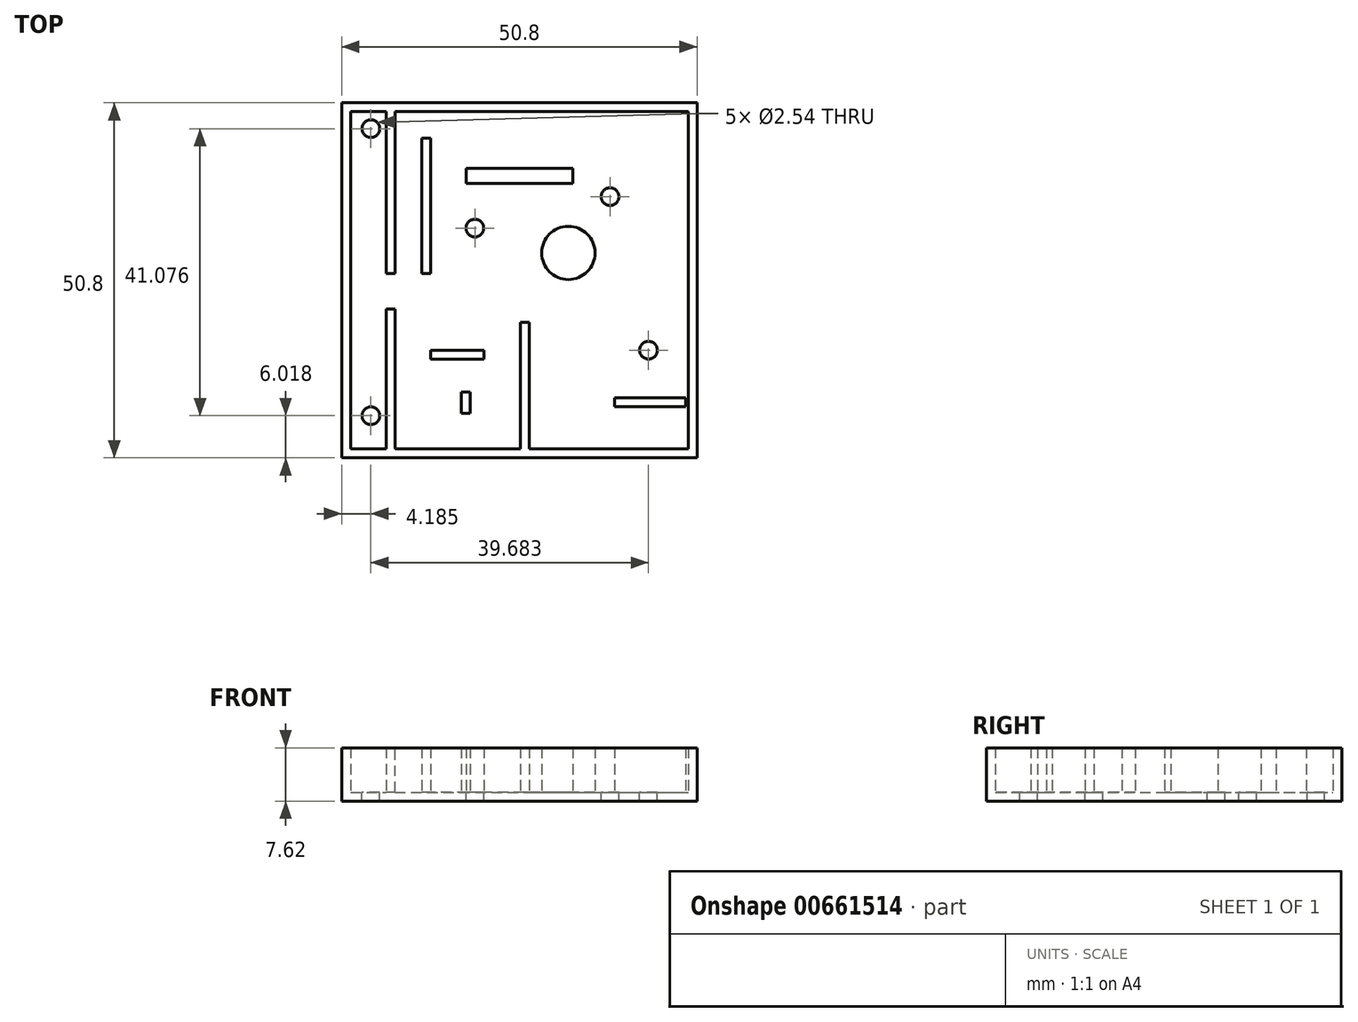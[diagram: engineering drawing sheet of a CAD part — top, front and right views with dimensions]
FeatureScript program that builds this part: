
annotation { "Feature Type Name" : "Feature", "Feature Type Description" : "" }
export const myFeature = defineFeature(function(context is Context, id is Id, definition is map)
    precondition{}
    {
        {
            var Q0;
            Q0=qCreatedBy(makeId("Top.planeOp"),FACE);
            var sketch = newSketch(context, id + "F0", { "sketchPlane" : qUnion([Q0])});
            skLineSegment(sketch, "E0.bottom", {"start": v(0, 0) * mm, "end": v(50.8, 0) * mm});
            skLineSegment(sketch, "E0.top", {"start": v(0, 50.8) * mm, "end": v(50.8, 50.8) * mm});
            skLineSegment(sketch, "E0.left", {"start": v(0, 0) * mm, "end": v(0, 50.8) * mm});
            skLineSegment(sketch, "E0.right", {"start": v(50.8, 0) * mm, "end": v(50.8, 50.8) * mm});
            skSolve(sketch);
        }
        {
            var Q0;
            Q0 = qSketchRegion(id + "F0", true);
            extrude(context, id + "F1", {"entities" : qUnion([Q0]), "depth" : 7.62 * mm, "offsetDistance" : 25.4 * mm});
        }
        {
            var Q0;
            Q0=makeQuery(id+"F1.opExtrude","CAP_FACE",FACE,{"disambiguationData":[OSD([sQuery(id+"F0.wireOp",EDGE,"E0.bottom"),sQuery(id+"F0.wireOp",EDGE,"E0.top"),sQuery(id+"F0.wireOp",EDGE,"E0.left"),sQuery(id+"F0.wireOp",EDGE,"E0.right")])],"isStart":false});
            shell(context, id + "F2", {"entities" : qUnion([Q0]), "thickness" : 1.27 * mm});
        }
        {
            var Q0;
            Q0=qCreatedBy(makeId("Top.planeOp"),FACE);
            var sketch = newSketch(context, id + "F3", { "sketchPlane" : qUnion([Q0])});
            skLineSegment(sketch, "E1", {"start": v(0, 0) * mm, "end": v(6.35, 0) * mm});
            skLineSegment(sketch, "E2.bottom", {"start": v(6.35, 0) * mm, "end": v(7.62, 0) * mm});
            skLineSegment(sketch, "E2.top", {"start": v(6.35, 21.3) * mm, "end": v(7.62, 21.3) * mm});
            skLineSegment(sketch, "E2.left", {"start": v(6.35, 0) * mm, "end": v(6.35, 21.3) * mm});
            skLineSegment(sketch, "E2.right", {"start": v(7.62, 0) * mm, "end": v(7.62, 21.3) * mm});
            skLineSegment(sketch, "E3", {"start": v(0, 50.65) * mm, "end": v(6.35, 50.65) * mm});
            skLineSegment(sketch, "E4.bottom", {"start": v(6.35, 50.65) * mm, "end": v(7.62, 50.65) * mm});
            skLineSegment(sketch, "E4.top", {"start": v(6.35, 26.38) * mm, "end": v(7.62, 26.38) * mm});
            skLineSegment(sketch, "E4.left", {"start": v(6.35, 50.65) * mm, "end": v(6.35, 26.38) * mm});
            skLineSegment(sketch, "E4.right", {"start": v(7.62, 50.65) * mm, "end": v(7.62, 26.38) * mm});
            skLineSegment(sketch, "E5.bottom", {"start": v(11.43, 45.72) * mm, "end": v(12.7, 45.72) * mm});
            skLineSegment(sketch, "E5.top", {"start": v(11.43, 26.38) * mm, "end": v(12.7, 26.38) * mm});
            skLineSegment(sketch, "E5.left", {"start": v(11.43, 45.72) * mm, "end": v(11.43, 26.38) * mm});
            skLineSegment(sketch, "E5.right", {"start": v(12.7, 45.72) * mm, "end": v(12.7, 26.38) * mm});
            skSolve(sketch);
        }
        {
            var Q0;
            Q0 = qSketchRegion(id + "F3", true);
            extrude(context, id + "F4", {"entities" : qUnion([Q0]), "operationType" : NewBodyOperationType.ADD, "depth" : 7.62 * mm, "offsetDistance" : 25.4 * mm});
        }
        {
            var Q0;
            Q0=qCreatedBy(makeId("Top.planeOp"),FACE);
            var sketch = newSketch(context, id + "F5", { "sketchPlane" : qUnion([Q0])});
            skLineSegment(sketch, "E6.bottom", {"start": v(49.15, 8.56) * mm, "end": v(39, 8.56) * mm});
            skLineSegment(sketch, "E6.top", {"start": v(49.15, 7.29) * mm, "end": v(39, 7.29) * mm});
            skLineSegment(sketch, "E6.left", {"start": v(49.15, 8.56) * mm, "end": v(49.15, 7.29) * mm});
            skLineSegment(sketch, "E6.right", {"start": v(39, 8.56) * mm, "end": v(39, 7.29) * mm});
            skLineSegment(sketch, "E7.bottom", {"start": v(17.78, 41.4) * mm, "end": v(33.02, 41.4) * mm});
            skLineSegment(sketch, "E7.top", {"start": v(17.78, 39.23) * mm, "end": v(33.02, 39.23) * mm});
            skLineSegment(sketch, "E7.left", {"start": v(17.78, 41.4) * mm, "end": v(17.78, 39.23) * mm});
            skLineSegment(sketch, "E7.right", {"start": v(33.02, 41.4) * mm, "end": v(33.02, 39.23) * mm});
            skLineSegment(sketch, "E8.bottom", {"start": v(12.7, 15.38) * mm, "end": v(20.32, 15.38) * mm});
            skLineSegment(sketch, "E8.top", {"start": v(12.7, 14.11) * mm, "end": v(20.32, 14.11) * mm});
            skLineSegment(sketch, "E8.left", {"start": v(12.7, 15.38) * mm, "end": v(12.7, 14.11) * mm});
            skLineSegment(sketch, "E8.right", {"start": v(20.32, 15.38) * mm, "end": v(20.32, 14.11) * mm});
            skCircle(sketch, "E9", {"center": v(32.4, 29.3) * mm, "radius": 3.81 * mm});
            skLineSegment(sketch, "E10.bottom", {"start": v(25.58, 19.38) * mm, "end": v(26.85, 19.38) * mm});
            skLineSegment(sketch, "E10.top", {"start": v(25.58, 0) * mm, "end": v(26.85, 0) * mm});
            skLineSegment(sketch, "E10.left", {"start": v(25.58, 19.38) * mm, "end": v(25.58, 0) * mm});
            skLineSegment(sketch, "E10.right", {"start": v(26.85, 19.38) * mm, "end": v(26.85, 0) * mm});
            skSolve(sketch);
        }
        {
            var Q0;
            Q0 = qSketchRegion(id + "F5", true);
            extrude(context, id + "F6", {"entities" : qUnion([Q0]), "operationType" : NewBodyOperationType.ADD, "depth" : 7.62 * mm, "offsetDistance" : 25.4 * mm});
        }
        {
            var Q0;
            Q0=qCreatedBy(makeId("Top.planeOp"),FACE);
            var sketch = newSketch(context, id + "F7", { "sketchPlane" : qUnion([Q0])});
            skCircle(sketch, "E11", {"center": v(3.86, 5.1) * mm, "radius": 0.64 * mm});
            skSolve(sketch);
        }
        {
            var Q0;
            Q0 = qSketchRegion(id + "F7", true);
            extrude(context, id + "F8", {"entities" : qUnion([Q0]), "operationType" : NewBodyOperationType.REMOVE, "oppositeDirection" : true, "depth" : 25.4 * mm, "offsetDistance" : 25.4 * mm});
        }
        {
            var Q0;
            Q0=makeQuery(id+"F2.opShell","OFFSET_FACE",FACE,{"disambiguationData":[OSD([sQuery(id+"F0.wireOp",EDGE,"E0.bottom"),sQuery(id+"F0.wireOp",EDGE,"E0.top"),sQuery(id+"F0.wireOp",EDGE,"E0.left"),sQuery(id+"F0.wireOp",EDGE,"E0.right")])]});
            var sketch = newSketch(context, id + "F9", { "sketchPlane" : qUnion([Q0])});
            skCircle(sketch, "E12", {"center": v(43.87, 15.38) * mm, "radius": 1.27 * mm});
            skSolve(sketch);
        }
        {
            var Q0;
            Q0 = qSketchRegion(id + "F9", true);
            extrude(context, id + "F10", {"entities" : qUnion([Q0]), "operationType" : NewBodyOperationType.REMOVE, "oppositeDirection" : true, "depth" : 25.4 * mm, "offsetDistance" : 25.4 * mm});
        }
        {
            var Q0;
            Q0=makeQuery(id+"F2.opShell","OFFSET_FACE",FACE,{"disambiguationData":[OSD([sQuery(id+"F0.wireOp",EDGE,"E0.bottom"),sQuery(id+"F0.wireOp",EDGE,"E0.top"),sQuery(id+"F0.wireOp",EDGE,"E0.left"),sQuery(id+"F0.wireOp",EDGE,"E0.right")])]});
            var sketch = newSketch(context, id + "F11", { "sketchPlane" : qUnion([Q0])});
            skCircle(sketch, "E13", {"center": v(38.37, 37.35) * mm, "radius": 1.27 * mm});
            skSolve(sketch);
        }
        {
            var Q0;
            Q0=makeQuery(id+"F11.imprint","IMPRINT",FACE,{"disambiguationData":[TD([[makeQuery(id+"F11.imprint","IMPRINT",EDGE,{"derivedFrom":sQuery(id+"F11.wireOp",EDGE,"E13")}),1.0]])]});
            extrude(context, id + "F12", {"entities" : qUnion([Q0]), "operationType" : NewBodyOperationType.REMOVE, "oppositeDirection" : true, "depth" : 25.4 * mm, "offsetDistance" : 25.4 * mm});
        }
        {
            var Q0;
            Q0=makeQuery(id+"F2.opShell","OFFSET_FACE",FACE,{"disambiguationData":[OSD([sQuery(id+"F0.wireOp",EDGE,"E0.bottom"),sQuery(id+"F0.wireOp",EDGE,"E0.top"),sQuery(id+"F0.wireOp",EDGE,"E0.left"),sQuery(id+"F0.wireOp",EDGE,"E0.right")])]});
            var sketch = newSketch(context, id + "F13", { "sketchPlane" : qUnion([Q0])});
            skCircle(sketch, "E14", {"center": v(19.05, 32.86) * mm, "radius": 1.27 * mm});
            skCircle(sketch, "E15", {"center": v(4.19, 47.1) * mm, "radius": 1.27 * mm});
            skCircle(sketch, "E16", {"center": v(4.19, 6.02) * mm, "radius": 1.27 * mm});
            skSolve(sketch);
        }
        {
            var Q0;
            Q0 = qSketchRegion(id + "F13", true);
            extrude(context, id + "F14", {"entities" : qUnion([Q0]), "operationType" : NewBodyOperationType.REMOVE, "oppositeDirection" : true, "depth" : 25.4 * mm, "offsetDistance" : 25.4 * mm});
        }
        {
            var Q0;
            Q0 = qSketchRegion(id + "F13", true);
            extrude(context, id + "F15", {"entities" : qUnion([Q0]), "operationType" : NewBodyOperationType.REMOVE, "oppositeDirection" : true, "depth" : 25.4 * mm, "offsetDistance" : 25.4 * mm});
        }
        {
            var Q0;
            Q0=qCreatedBy(makeId("Top.planeOp"),FACE);
            var sketch = newSketch(context, id + "F16", { "sketchPlane" : qUnion([Q0])});
            skLineSegment(sketch, "E17.bottom", {"start": v(17.1, 9.39) * mm, "end": v(18.38, 9.39) * mm});
            skLineSegment(sketch, "E17.top", {"start": v(17.1, 6.35) * mm, "end": v(18.38, 6.35) * mm});
            skLineSegment(sketch, "E17.left", {"start": v(17.1, 9.39) * mm, "end": v(17.1, 6.35) * mm});
            skLineSegment(sketch, "E17.right", {"start": v(18.38, 9.39) * mm, "end": v(18.38, 6.35) * mm});
            skSolve(sketch);
        }
        {
            var Q0;
            Q0 = qSketchRegion(id + "F16", true);
            extrude(context, id + "F17", {"entities" : qUnion([Q0]), "operationType" : NewBodyOperationType.ADD, "depth" : 7.62 * mm, "offsetDistance" : 25.4 * mm});
        }
    });
